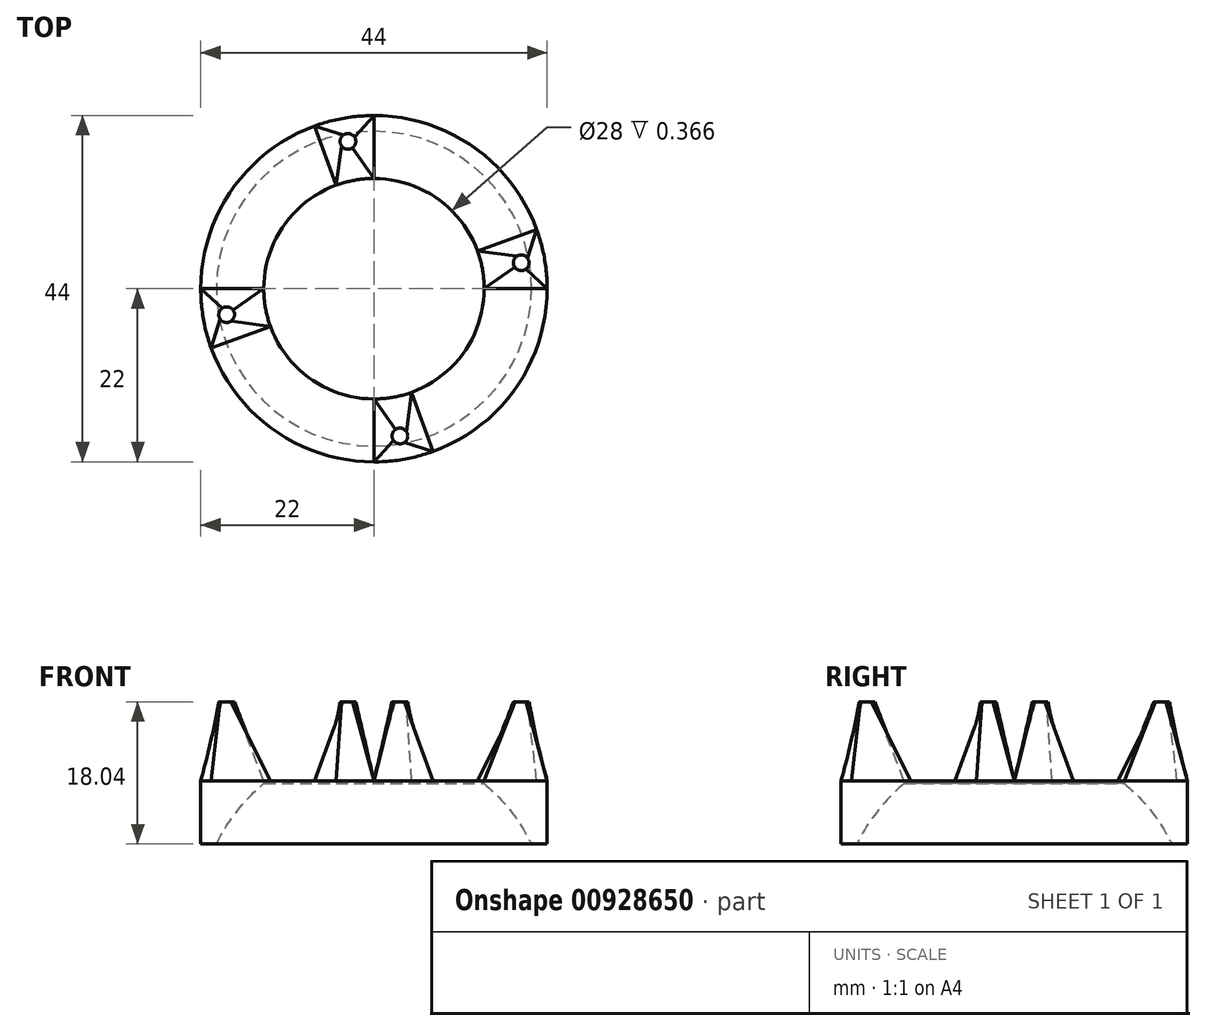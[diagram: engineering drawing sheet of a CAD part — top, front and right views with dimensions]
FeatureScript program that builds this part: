
annotation { "Feature Type Name" : "Feature", "Feature Type Description" : "" }
export const myFeature = defineFeature(function(context is Context, id is Id, definition is map)
    precondition{}
    {
        {
            var Q0;
            Q0=qCreatedBy(makeId("Front.planeOp"),FACE);
            var sketch = newSketch(context, id + "F0", { "sketchPlane" : qUnion([Q0])});
            skLineSegment(sketch, "E0", {"start": v(0, 0) * mm, "end": v(0, 52.54) * mm, "construction": true});
            skLineSegment(sketch, "E1.bottom", {"start": v(14, 0) * mm, "end": v(22, 0) * mm});
            skLineSegment(sketch, "E1.top", {"start": v(14, -8.04) * mm, "end": v(20, -8.04) * mm, "construction": true});
            skLineSegment(sketch, "E1.left", {"start": v(14, 0) * mm, "end": v(14, -0.37) * mm});
            skLineSegment(sketch, "E1.right", {"start": v(22, 0) * mm, "end": v(22, -8.04) * mm});
            skArc(sketch, "E2", {"start": v(14, -0.37) * mm, "mid": v(-19.63, -32.83) * mm, "end": v(20, -8.04) * mm, "construction": true});
            skArc(sketch, "E3", {"start": v(20, -8.04) * mm, "mid": v(17.4, -3.9) * mm, "end": v(14, -0.37) * mm});
            skLineSegment(sketch, "E4", {"start": v(20, -8.04) * mm, "end": v(22, -8.04) * mm});
            skLineSegment(sketch, "E5", {"start": v(14, -0.37) * mm, "end": v(14, -8.04) * mm, "construction": true});
            skPoint(sketch, "E6", {"position": v(18, 0) * mm});
            skSolve(sketch);
        }
        {
            var Q0;
            Q0=qSketchRegion(id+"F0",true);
            var Q1;
            Q1=sQuery(id+"F0.wireOp",EDGE,"E0");
            revolve(context, id + "F1", {"surfaceOperationType" : NewSurfaceOperationType.NEW, "entities" : qUnion([Q0]), "axis" : qUnion([Q1]), "revolveType" : RevolveType.TWO_DIRECTIONS, "angle" : 20 * degree, "angleBack" : 0 * degree});
        }
        {
            var Q0;
            Q0=makeQuery(id+"F1.opRevolve","SWEPT_BODY",BODY,{"disambiguationData":[OSD([sQuery(id+"F0.wireOp",EDGE,"E1.bottom"),sQuery(id+"F0.wireOp",EDGE,"E1.left"),sQuery(id+"F0.wireOp",EDGE,"E1.right"),sQuery(id+"F0.wireOp",EDGE,"E3"),sQuery(id+"F0.wireOp",EDGE,"E4")])]});
            var Q1;
            Q1=sQuery(id+"F0.wireOp",EDGE,"E0");
            circularPattern(context, id + "F2", {"entities" : qUnion([Q0]), "axis" : qUnion([Q1]), "angle" : 360 * degree, "instanceCount" : 4, "equalSpace" : true});
        }
        {
            var Q0;
            Q0=makeQuery(id+"F1.opRevolve","CAP_FACE",FACE,{"disambiguationData":[OSD([sQuery(id+"F0.wireOp",EDGE,"E1.bottom"),sQuery(id+"F0.wireOp",EDGE,"E1.left"),sQuery(id+"F0.wireOp",EDGE,"E1.right"),sQuery(id+"F0.wireOp",EDGE,"E3"),sQuery(id+"F0.wireOp",EDGE,"E4")])],"isStart":false});
            var sketch = newSketch(context, id + "F3", { "sketchPlane" : qUnion([Q0])});
            skSolve(sketch);
        }
        {
            var Q0;
            Q0=makeQuery(id+"F3.imprint","IMPRINT",FACE,{"disambiguationData":[TD([[makeQuery(id+"F3.imprint","IMPRINT",EDGE,{"derivedFrom":makeQuery(id+"F1.opRevolve","CAP_EDGE",EDGE,{"disambiguationData":[OSD([sQuery(id+"F0.wireOp",EDGE,"E1.bottom")])],"isStart":false})}),1.0]])]});
            var sketch = newSketch(context, id + "F4", { "sketchPlane" : qUnion([Q0])});
            skArc(sketch, "E7.0", {"start": v(-20, -8.04) * mm, "mid": v(-19.44, -6.97) * mm, "end": v(-18.83, -5.93) * mm});
            skArc(sketch, "E8", {"start": v(-18.83, -5.93) * mm, "mid": v(-16.63, -2.96) * mm, "end": v(-14, -0.37) * mm, "construction": true});
            skLineSegment(sketch, "E9.0", {"start": v(-22, 0) * mm, "end": v(-22, -8.04) * mm, "construction": true});
            skLineSegment(sketch, "E10", {"start": v(-18.83, -5.93) * mm, "end": v(-22, -5.93) * mm});
            skLineSegment(sketch, "E11", {"start": v(-22, -5.93) * mm, "end": v(-22, -8.04) * mm});
            skLineSegment(sketch, "E12", {"start": v(-22, -8.04) * mm, "end": v(-22, -5.93) * mm});
            skSolve(sketch);
        }
        {
            var Q0;
            Q0=makeQuery(id+"F4.imprint","IMPRINT",FACE,{"disambiguationData":[TD([[makeQuery(id+"F4.imprint","IMPRINT",EDGE,{"derivedFrom":sQuery(id+"F4.wireOp",EDGE,"E7.0")}),1.0]])]});
            var Q1;
            Q1=sQuery(id+"F0.wireOp",EDGE,"E0");
            revolve(context, id + "F5", {"surfaceOperationType" : NewSurfaceOperationType.NEW, "entities" : qUnion([Q0]), "axis" : qUnion([Q1]), "revolveType" : RevolveType.FULL});
        }
        {
            var Q0;
            Q0=makeQuery(id+"F1.opRevolve","SWEPT_BODY",BODY,{"disambiguationData":[OSD([sQuery(id+"F0.wireOp",EDGE,"E1.bottom"),sQuery(id+"F0.wireOp",EDGE,"E1.left"),sQuery(id+"F0.wireOp",EDGE,"E1.right"),sQuery(id+"F0.wireOp",EDGE,"E3"),sQuery(id+"F0.wireOp",EDGE,"E4")])]});
            var Q1;
            Q1=makeQuery(id+"F2.opPattern","COPY",BODY,{"derivedFrom":makeQuery(id+"F1.opRevolve","SWEPT_BODY",BODY,{"disambiguationData":[OSD([sQuery(id+"F0.wireOp",EDGE,"E1.bottom"),sQuery(id+"F0.wireOp",EDGE,"E1.left"),sQuery(id+"F0.wireOp",EDGE,"E1.right"),sQuery(id+"F0.wireOp",EDGE,"E3"),sQuery(id+"F0.wireOp",EDGE,"E4")])]}),"instanceName":"1"});
            var Q2;
            Q2=makeQuery(id+"F2.opPattern","COPY",BODY,{"derivedFrom":makeQuery(id+"F1.opRevolve","SWEPT_BODY",BODY,{"disambiguationData":[OSD([sQuery(id+"F0.wireOp",EDGE,"E1.bottom"),sQuery(id+"F0.wireOp",EDGE,"E1.left"),sQuery(id+"F0.wireOp",EDGE,"E1.right"),sQuery(id+"F0.wireOp",EDGE,"E3"),sQuery(id+"F0.wireOp",EDGE,"E4")])]}),"instanceName":"2"});
            var Q3;
            Q3=makeQuery(id+"F2.opPattern","COPY",BODY,{"derivedFrom":makeQuery(id+"F1.opRevolve","SWEPT_BODY",BODY,{"disambiguationData":[OSD([sQuery(id+"F0.wireOp",EDGE,"E1.bottom"),sQuery(id+"F0.wireOp",EDGE,"E1.left"),sQuery(id+"F0.wireOp",EDGE,"E1.right"),sQuery(id+"F0.wireOp",EDGE,"E3"),sQuery(id+"F0.wireOp",EDGE,"E4")])]}),"instanceName":"3"});
            var Q4;
            Q4=makeQuery(id+"F4MRWHUxZCtjSTf_1.opRevolve","SWEPT_BODY",BODY,{"disambiguationData":[OSD([sQuery(id+"F4.wireOp",EDGE,"fbh8r7x2-dHDZ-tj1j-kEbG-0VAMOkKymPMU"),sQuery(id+"F4.wireOp",EDGE,"M89PfBS0-vETp-Bnr5-nqTN-LByxgd289nsR"),sQuery(id+"F4.wireOp",EDGE,"wZ66k8tc-VATU-Sq5I-3KXL-PqXNBZ8GxHJM")])]});
            var Q5;
            Q5=makeQuery(id+"F5.opRevolve","SWEPT_BODY",BODY,{"disambiguationData":[OSD([sQuery(id+"F0.wireOp",EDGE,"E4"),sQuery(id+"F4.wireOp",EDGE,"E7.0"),sQuery(id+"F4.wireOp",EDGE,"E10"),sQuery(id+"F4.wireOp",EDGE,"E12")])]});
            booleanBodies(context, id + "F6", {"operationType" : BooleanOperationType.UNION, "tools" : qUnion([Q0, Q1, Q2, Q3, Q4, Q5])});
        }
        {
            var Q0;
            Q0=makeQuery(id+"F1.opRevolve","SWEPT_FACE",FACE,{"disambiguationData":[OSD([sQuery(id+"F0.wireOp",EDGE,"E1.bottom")])]});
            var sketch = newSketch(context, id + "F7", { "sketchPlane" : qUnion([Q0])});
            skLineSegment(sketch, "E13.0", {"start": v(14, 0) * mm, "end": v(22, 0) * mm});
            skLineSegment(sketch, "E13.1", {"start": v(13.16, 4.79) * mm, "end": v(20.67, 7.52) * mm});
            skArc(sketch, "E13.2", {"start": v(20.67, 7.52) * mm, "mid": v(21.67, 3.82) * mm, "end": v(22, 0) * mm});
            skArc(sketch, "E13.3", {"start": v(13.16, 4.79) * mm, "mid": v(13.79, 2.43) * mm, "end": v(14, 0) * mm});
            skSolve(sketch);
        }
        {
            var Q0;
            Q0=makeQuery(id+"F7.imprint","IMPRINT",FACE,{"disambiguationData":[TD([[makeQuery(id+"F7.imprint","IMPRINT",EDGE,{"derivedFrom":sQuery(id+"F7.wireOp",EDGE,"E13.0")}),1.0]])]});
            cPlane(context, id + "F8", {"entities" : qUnion([Q0]), "cplaneType" : CPlaneType.OFFSET, "offset" : 10 * mm, "width" : 150 * mm, "height" : 150 * mm});
        }
        {
            var Q0;
            Q0=qCreatedBy(id+"F8.planeOp",FACE);
            var sketch = newSketch(context, id + "F9", { "sketchPlane" : qUnion([Q0])});
            skPoint(sketch, "E14.0", {"position": v(13.79, 2.43) * mm});
            skLineSegment(sketch, "E15", {"start": v(0, 0) * mm, "end": v(18.71, 3.3) * mm, "construction": true});
            skCircle(sketch, "E16", {"center": v(18.71, 3.3) * mm, "radius": 1 * mm});
            skPoint(sketch, "E17", {"position": v(17.9, 3.87) * mm});
            skPoint(sketch, "E18", {"position": v(19.53, 2.73) * mm});
            skLineSegment(sketch, "E19", {"start": v(17.9, 3.87) * mm, "end": v(19.53, 2.73) * mm, "construction": true});
            skLineSegment(sketch, "E20", {"start": v(19.28, 4.12) * mm, "end": v(18.14, 2.48) * mm, "construction": true});
            skLineSegment(sketch, "E21", {"start": v(18.14, 2.48) * mm, "end": v(17.9, 3.87) * mm, "construction": true});
            skPoint(sketch, "E22", {"position": v(18.01, 3.18) * mm});
            skSolve(sketch);
        }
        {
            var Q1;
            Q1=makeQuery(id+"F7.imprint","IMPRINT",FACE,{"disambiguationData":[TD([[makeQuery(id+"F7.imprint","IMPRINT",EDGE,{"derivedFrom":sQuery(id+"F7.wireOp",EDGE,"E13.0")}),1.0]])]});
            var Q2;
            Q2=makeQuery(id+"F9.imprint","IMPRINT",FACE,{"disambiguationData":[TD([[makeQuery(id+"F9.imprint","IMPRINT",EDGE,{"derivedFrom":sQuery(id+"F9.wireOp",EDGE,"E16")}),1.0]])]});
            loft(context, id + "F10", {"sheetProfilesArray" : [{ "sheetProfileEntities" : qUnion([Q1]) }, { "sheetProfileEntities" : qUnion([Q2]) }]});
        }
        {
            var Q0;
            Q0=makeQuery(id+"F10.opLoft","SWEPT_BODY",BODY,{"disambiguationData":[OSD([makeQuery(id+"F7.imprint","IMPRINT",FACE,{"disambiguationData":[TD([[makeQuery(id+"F7.imprint","IMPRINT",EDGE,{"derivedFrom":sQuery(id+"F7.wireOp",EDGE,"E13.0")}),1.0]])]}),makeQuery(id+"F9.imprint","IMPRINT",FACE,{"disambiguationData":[TD([[makeQuery(id+"F9.imprint","IMPRINT",EDGE,{"derivedFrom":sQuery(id+"F9.wireOp",EDGE,"E16")}),1.0]])]})])]});
            var Q1;
            Q1=sQuery(id+"F0.wireOp",EDGE,"E0");
            circularPattern(context, id + "F11", {"entities" : qUnion([Q0]), "axis" : qUnion([Q1]), "angle" : 360 * degree, "instanceCount" : 4, "equalSpace" : true});
        }
        {
            var Q0;
            Q0=makeQuery(id+"F1.opRevolve","SWEPT_BODY",BODY,{"disambiguationData":[OSD([sQuery(id+"F0.wireOp",EDGE,"E1.bottom"),sQuery(id+"F0.wireOp",EDGE,"E1.left"),sQuery(id+"F0.wireOp",EDGE,"E1.right"),sQuery(id+"F0.wireOp",EDGE,"E3"),sQuery(id+"F0.wireOp",EDGE,"E4")])]});
            var Q1;
            Q1=makeQuery(id+"F10.opLoft","SWEPT_BODY",BODY,{"disambiguationData":[OSD([makeQuery(id+"F7.imprint","IMPRINT",FACE,{"disambiguationData":[TD([[makeQuery(id+"F7.imprint","IMPRINT",EDGE,{"derivedFrom":sQuery(id+"F7.wireOp",EDGE,"E13.0")}),1.0]])]}),makeQuery(id+"F9.imprint","IMPRINT",FACE,{"disambiguationData":[TD([[makeQuery(id+"F9.imprint","IMPRINT",EDGE,{"derivedFrom":sQuery(id+"F9.wireOp",EDGE,"E16")}),1.0]])]})])]});
            var Q2;
            Q2=makeQuery(id+"F11.opPattern","COPY",BODY,{"derivedFrom":makeQuery(id+"F10.opLoft","SWEPT_BODY",BODY,{"disambiguationData":[OSD([makeQuery(id+"F7.imprint","IMPRINT",FACE,{"disambiguationData":[TD([[makeQuery(id+"F7.imprint","IMPRINT",EDGE,{"derivedFrom":sQuery(id+"F7.wireOp",EDGE,"E13.0")}),1.0]])]}),makeQuery(id+"F9.imprint","IMPRINT",FACE,{"disambiguationData":[TD([[makeQuery(id+"F9.imprint","IMPRINT",EDGE,{"derivedFrom":sQuery(id+"F9.wireOp",EDGE,"E16")}),1.0]])]})])]}),"instanceName":"1"});
            var Q3;
            Q3=makeQuery(id+"F11.opPattern","COPY",BODY,{"derivedFrom":makeQuery(id+"F10.opLoft","SWEPT_BODY",BODY,{"disambiguationData":[OSD([makeQuery(id+"F7.imprint","IMPRINT",FACE,{"disambiguationData":[TD([[makeQuery(id+"F7.imprint","IMPRINT",EDGE,{"derivedFrom":sQuery(id+"F7.wireOp",EDGE,"E13.0")}),1.0]])]}),makeQuery(id+"F9.imprint","IMPRINT",FACE,{"disambiguationData":[TD([[makeQuery(id+"F9.imprint","IMPRINT",EDGE,{"derivedFrom":sQuery(id+"F9.wireOp",EDGE,"E16")}),1.0]])]})])]}),"instanceName":"2"});
            var Q4;
            Q4=makeQuery(id+"F11.opPattern","COPY",BODY,{"derivedFrom":makeQuery(id+"F10.opLoft","SWEPT_BODY",BODY,{"disambiguationData":[OSD([makeQuery(id+"F7.imprint","IMPRINT",FACE,{"disambiguationData":[TD([[makeQuery(id+"F7.imprint","IMPRINT",EDGE,{"derivedFrom":sQuery(id+"F7.wireOp",EDGE,"E13.0")}),1.0]])]}),makeQuery(id+"F9.imprint","IMPRINT",FACE,{"disambiguationData":[TD([[makeQuery(id+"F9.imprint","IMPRINT",EDGE,{"derivedFrom":sQuery(id+"F9.wireOp",EDGE,"E16")}),1.0]])]})])]}),"instanceName":"3"});
            booleanBodies(context, id + "F12", {"operationType" : BooleanOperationType.UNION, "tools" : qUnion([Q0, Q1, Q2, Q3, Q4])});
        }
        {
            var Q0;
            Q0=makeQuery(id+"F1.opRevolve","CAP_FACE",FACE,{"disambiguationData":[OSD([sQuery(id+"F0.wireOp",EDGE,"E1.bottom"),sQuery(id+"F0.wireOp",EDGE,"E1.left"),sQuery(id+"F0.wireOp",EDGE,"E1.right"),sQuery(id+"F0.wireOp",EDGE,"E3"),sQuery(id+"F0.wireOp",EDGE,"E4")])],"isStart":true});
            var Q1;
            Q1=sQuery(id+"F0.wireOp",EDGE,"E0");
            revolve(context, id + "F13", {"operationType" : NewBodyOperationType.ADD, "surfaceOperationType" : NewSurfaceOperationType.NEW, "entities" : qUnion([Q0]), "axis" : qUnion([Q1]), "revolveType" : RevolveType.FULL});
        }
    });
